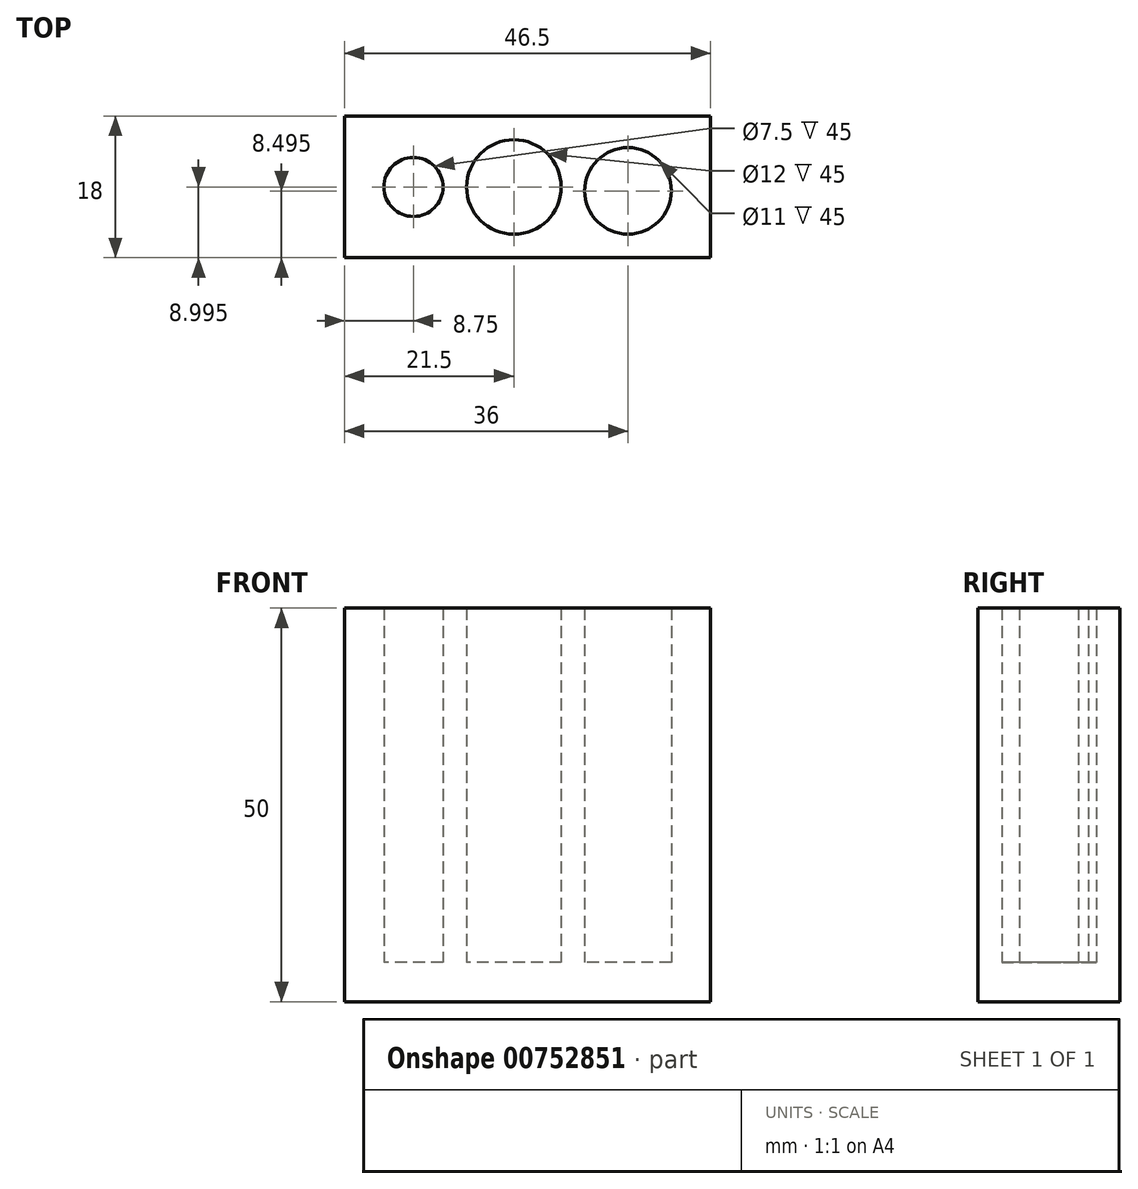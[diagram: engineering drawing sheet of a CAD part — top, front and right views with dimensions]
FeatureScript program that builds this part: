
annotation { "Feature Type Name" : "Feature", "Feature Type Description" : "" }
export const myFeature = defineFeature(function(context is Context, id is Id, definition is map)
    precondition{}
    {
        {
            var Q0;
            Q0=qCreatedBy(makeId("Top.planeOp"),FACE);
            var sketch = newSketch(context, id + "F0", { "sketchPlane" : qUnion([Q0])});
            skCircle(sketch, "E0", {"center": v(-54.88, 32.15) * mm, "radius": 3.75 * mm});
            skCircle(sketch, "E1", {"center": v(-42.13, 32.15) * mm, "radius": 6 * mm});
            skCircle(sketch, "E2", {"center": v(-27.63, 31.65) * mm, "radius": 5.5 * mm});
            skLineSegment(sketch, "E3.bottom", {"start": v(-63.63, 41.15) * mm, "end": v(-17.13, 41.15) * mm});
            skLineSegment(sketch, "E3.top", {"start": v(-63.63, 23.15) * mm, "end": v(-17.13, 23.15) * mm});
            skLineSegment(sketch, "E3.left", {"start": v(-63.63, 41.15) * mm, "end": v(-63.63, 23.15) * mm});
            skLineSegment(sketch, "E3.right", {"start": v(-17.13, 41.15) * mm, "end": v(-17.13, 23.15) * mm});
            skSolve(sketch);
        }
        {
            var Q0;
            Q0=makeQuery(id+"F0.imprint","IMPRINT",FACE,{"disambiguationData":[TD([[makeQuery(id+"F0.imprint","IMPRINT",EDGE,{"derivedFrom":sQuery(id+"F0.wireOp",EDGE,"E0")}),-1.0]])]});
            extrude(context, id + "F1", {"entities" : qUnion([Q0]), "depth" : 50 * mm, "offsetDistance" : 25 * mm});
        }
        {
            var Q0;
            Q0=makeQuery(id+"F0.imprint","IMPRINT",FACE,{"disambiguationData":[TD([[makeQuery(id+"F0.imprint","IMPRINT",EDGE,{"derivedFrom":sQuery(id+"F0.wireOp",EDGE,"E2")}),1.0]])]});
            var Q1;
            Q1=makeQuery(id+"F0.imprint","IMPRINT",FACE,{"disambiguationData":[TD([[makeQuery(id+"F0.imprint","IMPRINT",EDGE,{"derivedFrom":sQuery(id+"F0.wireOp",EDGE,"E1")}),1.0]])]});
            var Q2;
            Q2=makeQuery(id+"F0.imprint","IMPRINT",FACE,{"disambiguationData":[TD([[makeQuery(id+"F0.imprint","IMPRINT",EDGE,{"derivedFrom":sQuery(id+"F0.wireOp",EDGE,"E0")}),1.0]])]});
            extrude(context, id + "F2", {"entities" : qUnion([Q0, Q1, Q2]), "operationType" : NewBodyOperationType.ADD, "depth" : 5 * mm, "offsetDistance" : 25 * mm});
        }
    });
